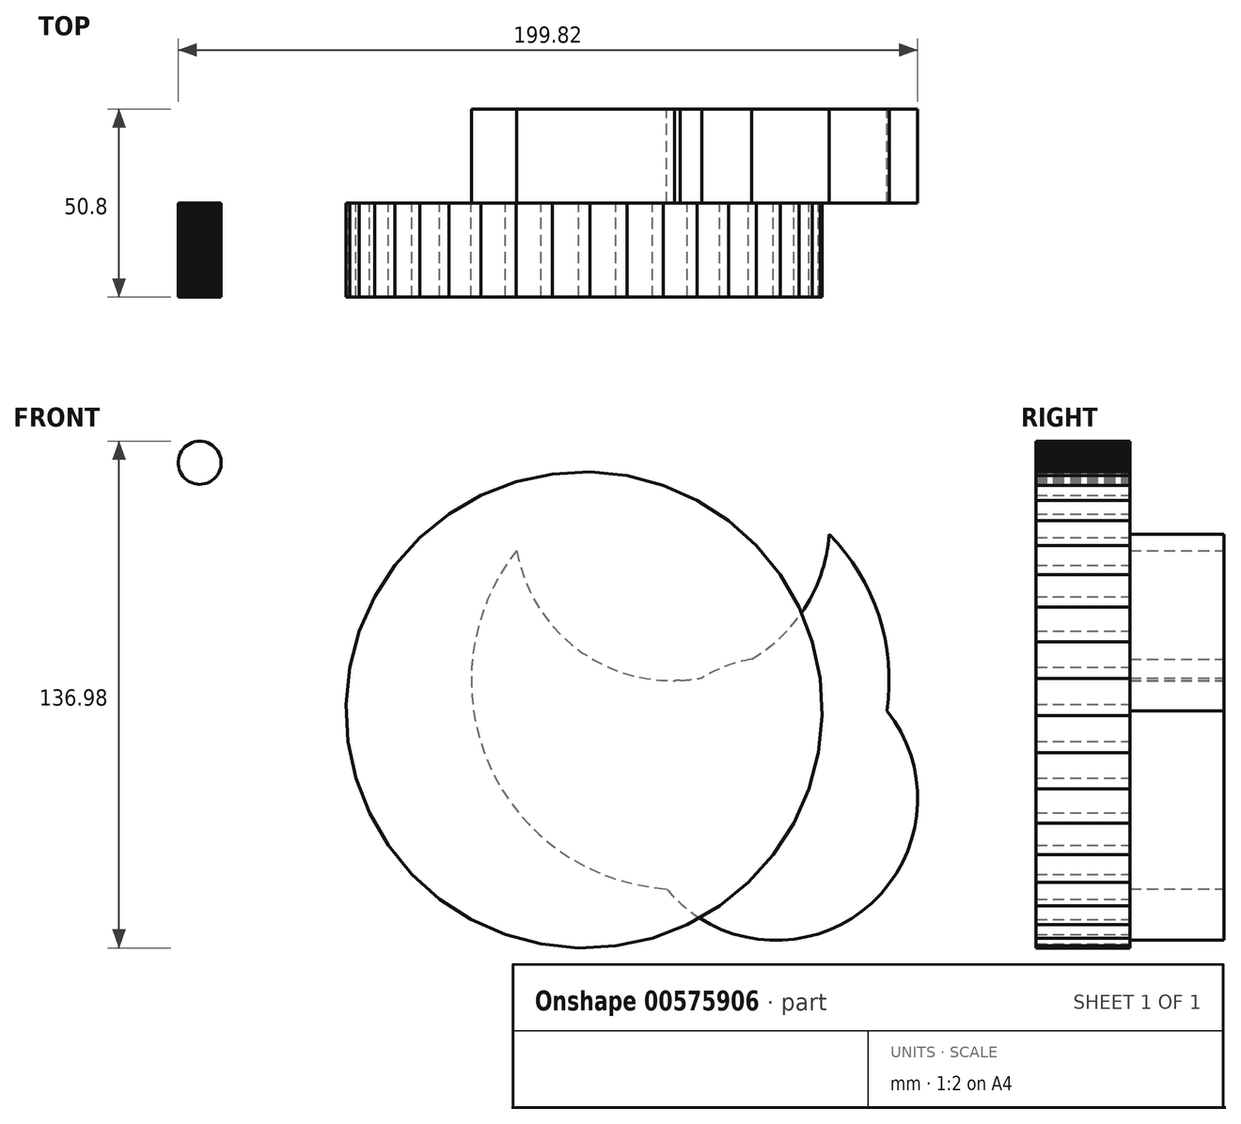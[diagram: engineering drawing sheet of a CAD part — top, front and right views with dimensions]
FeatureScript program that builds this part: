
annotation { "Feature Type Name" : "Feature", "Feature Type Description" : "" }
export const myFeature = defineFeature(function(context is Context, id is Id, definition is map)
    precondition{}
    {
        {
            var Q0;
            Q0=qCreatedBy(makeId("Front.planeOp"),FACE);
            var sketch = newSketch(context, id + "F0", { "sketchPlane" : qUnion([Q0])});
            skArc(sketch, "E0", {"start": v(-57.68, 38.84) * mm, "mid": v(-10.56, -52.67) * mm, "end": v(26.75, 43.26) * mm});
            skArc(sketch, "E1", {"start": v(-57.68, 38.84) * mm, "mid": v(-13.51, 3.7) * mm, "end": v(26.75, 43.26) * mm});
            skArc(sketch, "E2", {"start": v(-13.51, 3.7) * mm, "mid": v(-41.54, -22.74) * mm, "end": v(-17.21, -52.63) * mm});
            skArc(sketch, "E3", {"start": v(-17.21, -52.63) * mm, "mid": v(50.54, -30.95) * mm, "end": v(-13.51, 0) * mm});
            skSolve(sketch);
        }
        {
            var Q0;
            Q0 = qSketchRegion(id + "F0", true);
            extrude(context, id + "F1", {"entities" : qUnion([Q0]), "depth" : 25.4 * mm, "offsetDistance" : 25.4 * mm});
        }
        {
            var Q0;
            Q0=makeQuery(id+"F1.opExtrude","CAP_FACE",FACE,{"disambiguationData":[OSD([sQuery(id+"F0.wireOp",EDGE,"E0"),sQuery(id+"F0.wireOp",EDGE,"E1"),sQuery(id+"F0.wireOp",EDGE,"E2"),sQuery(id+"F0.wireOp",EDGE,"E3")])],"isStart":false});
            var sketch = newSketch(context, id + "F2", { "sketchPlane" : qUnion([Q0])});
            skCircle(sketch, "E4.cCircle", {"center": v(-39.48, -4.26) * mm, "radius": 64.16 * mm, "construction": true});
            skLineSegment(sketch, "E4.0", {"start": v(-11.64, -62.3) * mm, "end": v(-21.06, -65.93) * mm});
            skLineSegment(sketch, "E4.1", {"start": v(-21.06, -65.93) * mm, "end": v(-30.94, -68.06) * mm});
            skLineSegment(sketch, "E4.2", {"start": v(-30.94, -68.06) * mm, "end": v(-41.02, -68.6) * mm});
            skLineSegment(sketch, "E4.3", {"start": v(-41.02, -68.6) * mm, "end": v(-51.07, -67.57) * mm});
            skLineSegment(sketch, "E4.4", {"start": v(-51.07, -67.57) * mm, "end": v(-60.83, -64.98) * mm});
            skLineSegment(sketch, "E4.5", {"start": v(-60.83, -64.98) * mm, "end": v(-70.07, -60.9) * mm});
            skLineSegment(sketch, "E4.6", {"start": v(-70.07, -60.9) * mm, "end": v(-78.55, -55.41) * mm});
            skLineSegment(sketch, "E4.7", {"start": v(-78.55, -55.41) * mm, "end": v(-86.07, -48.67) * mm});
            skLineSegment(sketch, "E4.8", {"start": v(-86.07, -48.67) * mm, "end": v(-92.44, -40.84) * mm});
            skLineSegment(sketch, "E4.9", {"start": v(-92.44, -40.84) * mm, "end": v(-97.51, -32.1) * mm});
            skLineSegment(sketch, "E4.10", {"start": v(-97.51, -32.1) * mm, "end": v(-101.15, -22.68) * mm});
            skLineSegment(sketch, "E4.11", {"start": v(-101.15, -22.68) * mm, "end": v(-103.27, -12.8) * mm});
            skLineSegment(sketch, "E4.12", {"start": v(-103.27, -12.8) * mm, "end": v(-103.83, -2.72) * mm});
            skLineSegment(sketch, "E4.13", {"start": v(-103.83, -2.72) * mm, "end": v(-102.8, 7.32) * mm});
            skLineSegment(sketch, "E4.14", {"start": v(-102.8, 7.32) * mm, "end": v(-100.2, 17.09) * mm});
            skLineSegment(sketch, "E4.15", {"start": v(-100.2, 17.09) * mm, "end": v(-96.11, 26.32) * mm});
            skLineSegment(sketch, "E4.16", {"start": v(-96.11, 26.32) * mm, "end": v(-90.63, 34.8) * mm});
            skLineSegment(sketch, "E4.17", {"start": v(-90.63, 34.8) * mm, "end": v(-83.9, 42.32) * mm});
            skLineSegment(sketch, "E4.18", {"start": v(-83.9, 42.32) * mm, "end": v(-76.06, 48.7) * mm});
            skLineSegment(sketch, "E4.19", {"start": v(-76.06, 48.7) * mm, "end": v(-67.32, 53.77) * mm});
            skLineSegment(sketch, "E4.20", {"start": v(-67.32, 53.77) * mm, "end": v(-57.9, 57.4) * mm});
            skLineSegment(sketch, "E4.21", {"start": v(-57.9, 57.4) * mm, "end": v(-48.03, 59.53) * mm});
            skLineSegment(sketch, "E4.22", {"start": v(-48.03, 59.53) * mm, "end": v(-37.94, 60.08) * mm});
            skLineSegment(sketch, "E4.23", {"start": v(-37.94, 60.08) * mm, "end": v(-27.9, 59.05) * mm});
            skLineSegment(sketch, "E4.24", {"start": v(-27.9, 59.05) * mm, "end": v(-18.13, 56.46) * mm});
            skLineSegment(sketch, "E4.25", {"start": v(-18.13, 56.46) * mm, "end": v(-8.9, 52.37) * mm});
            skLineSegment(sketch, "E4.26", {"start": v(-8.9, 52.37) * mm, "end": v(-0.41, 46.89) * mm});
            skLineSegment(sketch, "E4.27", {"start": v(-0.41, 46.89) * mm, "end": v(7.1, 40.15) * mm});
            skLineSegment(sketch, "E4.28", {"start": v(7.1, 40.15) * mm, "end": v(13.48, 32.31) * mm});
            skLineSegment(sketch, "E4.29", {"start": v(13.48, 32.31) * mm, "end": v(18.55, 23.58) * mm});
            skLineSegment(sketch, "E4.30", {"start": v(18.55, 23.58) * mm, "end": v(22.2, 14.16) * mm});
            skLineSegment(sketch, "E4.31", {"start": v(22.2, 14.16) * mm, "end": v(24.31, 4.28) * mm});
            skLineSegment(sketch, "E4.32", {"start": v(24.31, 4.28) * mm, "end": v(24.86, -5.8) * mm});
            skLineSegment(sketch, "E4.33", {"start": v(24.86, -5.8) * mm, "end": v(23.83, -15.85) * mm});
            skLineSegment(sketch, "E4.34", {"start": v(23.83, -15.85) * mm, "end": v(21.24, -25.61) * mm});
            skLineSegment(sketch, "E4.35", {"start": v(21.24, -25.61) * mm, "end": v(17.15, -34.85) * mm});
            skLineSegment(sketch, "E4.36", {"start": v(17.15, -34.85) * mm, "end": v(11.67, -43.33) * mm});
            skLineSegment(sketch, "E4.37", {"start": v(11.67, -43.33) * mm, "end": v(4.93, -50.85) * mm});
            skLineSegment(sketch, "E4.38", {"start": v(4.93, -50.85) * mm, "end": v(-2.9, -57.22) * mm});
            skLineSegment(sketch, "E4.39", {"start": v(-2.9, -57.22) * mm, "end": v(-11.64, -62.3) * mm});
            skPoint(sketch, "E4.0.midPoint", {"position": v(-16.35, -64.11) * mm});
            skCircle(sketch, "E5.cCircle", {"center": v(-143.38, 62.55) * mm, "radius": 5.8 * mm, "construction": true});
            skLineSegment(sketch, "E5.0", {"start": v(-139.4, 58.3) * mm, "end": v(-139.97, 57.83) * mm});
            skLineSegment(sketch, "E5.1", {"start": v(-139.97, 57.83) * mm, "end": v(-140.59, 57.44) * mm});
            skLineSegment(sketch, "E5.2", {"start": v(-140.59, 57.44) * mm, "end": v(-141.25, 57.13) * mm});
            skLineSegment(sketch, "E5.3", {"start": v(-141.25, 57.13) * mm, "end": v(-141.95, 56.91) * mm});
            skLineSegment(sketch, "E5.4", {"start": v(-141.95, 56.91) * mm, "end": v(-142.66, 56.78) * mm});
            skLineSegment(sketch, "E5.5", {"start": v(-142.66, 56.78) * mm, "end": v(-143.4, 56.73) * mm});
            skLineSegment(sketch, "E5.6", {"start": v(-143.4, 56.73) * mm, "end": v(-144.12, 56.78) * mm});
            skLineSegment(sketch, "E5.7", {"start": v(-144.12, 56.78) * mm, "end": v(-144.84, 56.92) * mm});
            skLineSegment(sketch, "E5.8", {"start": v(-144.84, 56.92) * mm, "end": v(-145.54, 57.15) * mm});
            skLineSegment(sketch, "E5.9", {"start": v(-145.54, 57.15) * mm, "end": v(-146.2, 57.46) * mm});
            skLineSegment(sketch, "E5.10", {"start": v(-146.2, 57.46) * mm, "end": v(-146.81, 57.85) * mm});
            skLineSegment(sketch, "E5.11", {"start": v(-146.81, 57.85) * mm, "end": v(-147.37, 58.32) * mm});
            skLineSegment(sketch, "E5.12", {"start": v(-147.37, 58.32) * mm, "end": v(-147.87, 58.86) * mm});
            skLineSegment(sketch, "E5.13", {"start": v(-147.87, 58.86) * mm, "end": v(-148.3, 59.45) * mm});
            skLineSegment(sketch, "E5.14", {"start": v(-148.3, 59.45) * mm, "end": v(-148.65, 60.09) * mm});
            skLineSegment(sketch, "E5.15", {"start": v(-148.65, 60.09) * mm, "end": v(-148.92, 60.77) * mm});
            skLineSegment(sketch, "E5.16", {"start": v(-148.92, 60.77) * mm, "end": v(-149.1, 61.48) * mm});
            skLineSegment(sketch, "E5.17", {"start": v(-149.1, 61.48) * mm, "end": v(-149.19, 62.2) * mm});
            skLineSegment(sketch, "E5.18", {"start": v(-149.19, 62.2) * mm, "end": v(-149.19, 62.94) * mm});
            skLineSegment(sketch, "E5.19", {"start": v(-149.19, 62.94) * mm, "end": v(-149.1, 63.66) * mm});
            skLineSegment(sketch, "E5.20", {"start": v(-149.1, 63.66) * mm, "end": v(-148.9, 64.37) * mm});
            skLineSegment(sketch, "E5.21", {"start": v(-148.9, 64.37) * mm, "end": v(-148.64, 65.05) * mm});
            skLineSegment(sketch, "E5.22", {"start": v(-148.64, 65.05) * mm, "end": v(-148.28, 65.69) * mm});
            skLineSegment(sketch, "E5.23", {"start": v(-148.28, 65.69) * mm, "end": v(-147.85, 66.28) * mm});
            skLineSegment(sketch, "E5.24", {"start": v(-147.85, 66.28) * mm, "end": v(-147.35, 66.8) * mm});
            skLineSegment(sketch, "E5.25", {"start": v(-147.35, 66.8) * mm, "end": v(-146.78, 67.27) * mm});
            skLineSegment(sketch, "E5.26", {"start": v(-146.78, 67.27) * mm, "end": v(-146.17, 67.66) * mm});
            skLineSegment(sketch, "E5.27", {"start": v(-146.17, 67.66) * mm, "end": v(-145.5, 67.97) * mm});
            skLineSegment(sketch, "E5.28", {"start": v(-145.5, 67.97) * mm, "end": v(-144.8, 68.2) * mm});
            skLineSegment(sketch, "E5.29", {"start": v(-144.8, 68.2) * mm, "end": v(-144.09, 68.33) * mm});
            skLineSegment(sketch, "E5.30", {"start": v(-144.09, 68.33) * mm, "end": v(-143.36, 68.37) * mm});
            skLineSegment(sketch, "E5.31", {"start": v(-143.36, 68.37) * mm, "end": v(-142.63, 68.33) * mm});
            skLineSegment(sketch, "E5.32", {"start": v(-142.63, 68.33) * mm, "end": v(-141.91, 68.19) * mm});
            skLineSegment(sketch, "E5.33", {"start": v(-141.91, 68.19) * mm, "end": v(-141.22, 67.96) * mm});
            skLineSegment(sketch, "E5.34", {"start": v(-141.22, 67.96) * mm, "end": v(-140.56, 67.65) * mm});
            skLineSegment(sketch, "E5.35", {"start": v(-140.56, 67.65) * mm, "end": v(-139.94, 67.25) * mm});
            skLineSegment(sketch, "E5.36", {"start": v(-139.94, 67.25) * mm, "end": v(-139.38, 66.78) * mm});
            skLineSegment(sketch, "E5.37", {"start": v(-139.38, 66.78) * mm, "end": v(-138.88, 66.25) * mm});
            skLineSegment(sketch, "E5.38", {"start": v(-138.88, 66.25) * mm, "end": v(-138.45, 65.66) * mm});
            skLineSegment(sketch, "E5.39", {"start": v(-138.45, 65.66) * mm, "end": v(-138.1, 65.02) * mm});
            skLineSegment(sketch, "E5.40", {"start": v(-138.1, 65.02) * mm, "end": v(-137.84, 64.34) * mm});
            skLineSegment(sketch, "E5.41", {"start": v(-137.84, 64.34) * mm, "end": v(-137.66, 63.63) * mm});
            skLineSegment(sketch, "E5.42", {"start": v(-137.66, 63.63) * mm, "end": v(-137.57, 62.9) * mm});
            skLineSegment(sketch, "E5.43", {"start": v(-137.57, 62.9) * mm, "end": v(-137.57, 62.17) * mm});
            skLineSegment(sketch, "E5.44", {"start": v(-137.57, 62.17) * mm, "end": v(-137.66, 61.45) * mm});
            skLineSegment(sketch, "E5.45", {"start": v(-137.66, 61.45) * mm, "end": v(-137.85, 60.74) * mm});
            skLineSegment(sketch, "E5.46", {"start": v(-137.85, 60.74) * mm, "end": v(-138.12, 60.06) * mm});
            skLineSegment(sketch, "E5.47", {"start": v(-138.12, 60.06) * mm, "end": v(-138.47, 59.42) * mm});
            skLineSegment(sketch, "E5.48", {"start": v(-138.47, 59.42) * mm, "end": v(-138.9, 58.83) * mm});
            skLineSegment(sketch, "E5.49", {"start": v(-138.9, 58.83) * mm, "end": v(-139.4, 58.3) * mm});
            skPoint(sketch, "E5.0.midPoint", {"position": v(-139.69, 58.07) * mm});
            skSolve(sketch);
        }
        {
            var Q0;
            Q0 = qSketchRegion(id + "F2", true);
            extrude(context, id + "F3", {"entities" : qUnion([Q0]), "operationType" : NewBodyOperationType.ADD, "depth" : 25.4 * mm, "offsetDistance" : 25.4 * mm});
        }
    });
